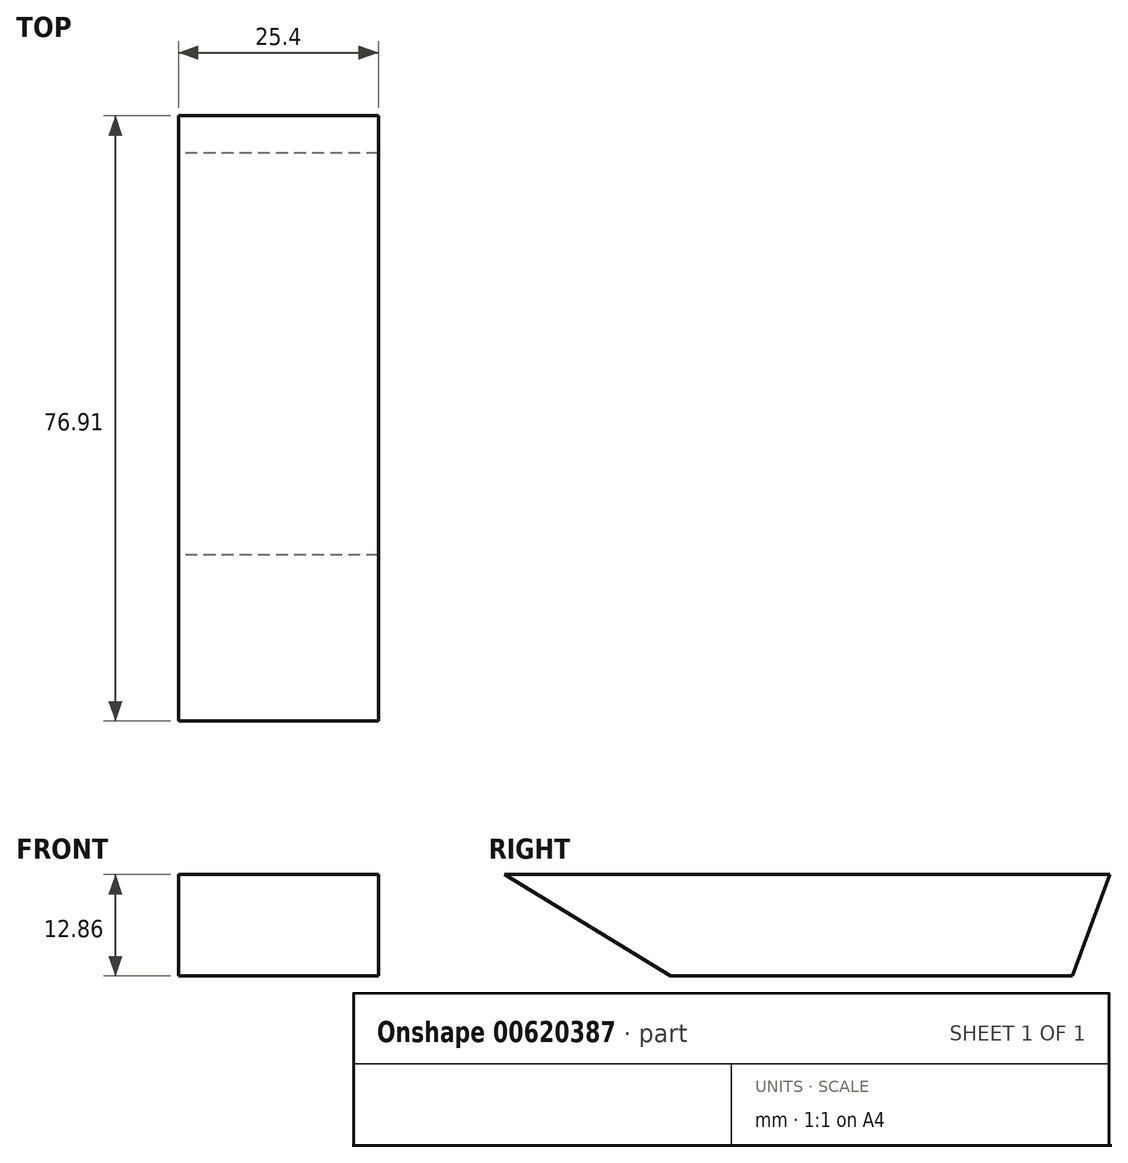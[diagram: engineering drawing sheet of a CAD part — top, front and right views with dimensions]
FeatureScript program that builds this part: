
annotation { "Feature Type Name" : "Feature", "Feature Type Description" : "" }
export const myFeature = defineFeature(function(context is Context, id is Id, definition is map)
    precondition{}
    {
        {
            var Q0;
            Q0=qCreatedBy(makeId("Right.planeOp"),FACE);
            var sketch = newSketch(context, id + "F0", { "sketchPlane" : qUnion([Q0])});
            skLineSegment(sketch, "E0", {"start": v(0, 0) * mm, "end": v(-51.04, 0) * mm});
            skLineSegment(sketch, "E1", {"start": v(-51.04, 0) * mm, "end": v(-72.14, 12.86) * mm});
            skLineSegment(sketch, "E2", {"start": v(-72.14, 12.86) * mm, "end": v(4.77, 12.86) * mm});
            skLineSegment(sketch, "E3", {"start": v(4.77, 12.86) * mm, "end": v(0, 0) * mm});
            skSolve(sketch);
        }
        {
            var Q0;
            Q0=makeQuery(id+"F0.imprint","IMPRINT",FACE,{"disambiguationData":[TD([[makeQuery(id+"F0.imprint","IMPRINT",EDGE,{"derivedFrom":sQuery(id+"F0.wireOp",EDGE,"E0")}),-1.0]])]});
            extrude(context, id + "F1", {"entities" : qUnion([Q0]), "depth" : 25.4 * mm, "offsetDistance" : 25.4 * mm});
        }
    });
